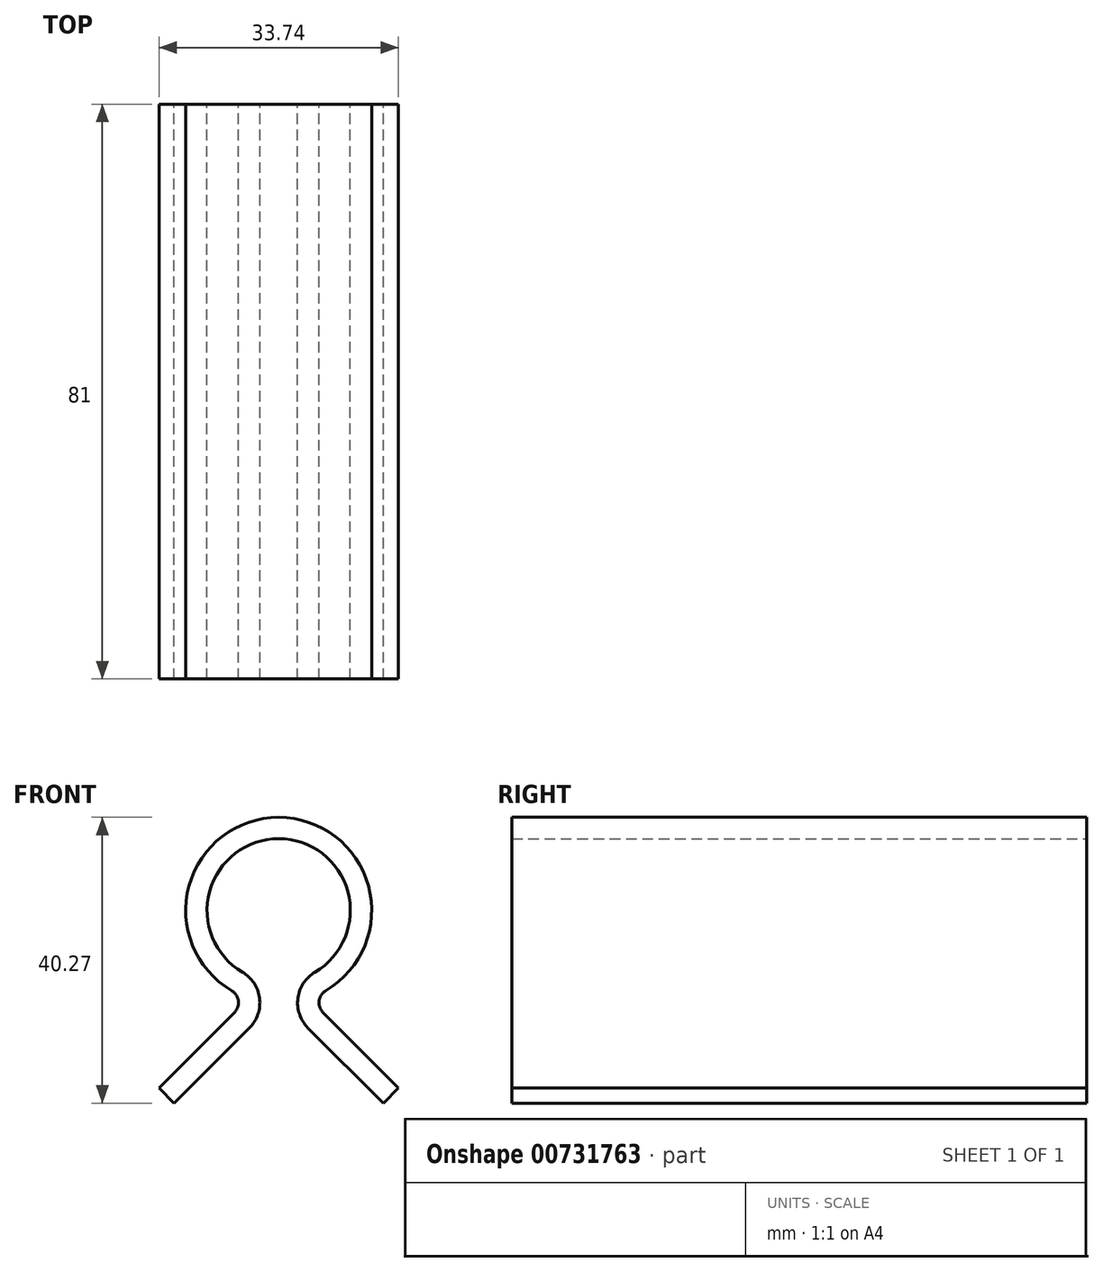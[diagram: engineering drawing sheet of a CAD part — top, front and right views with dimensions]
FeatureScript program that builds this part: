
annotation { "Feature Type Name" : "Feature", "Feature Type Description" : "" }
export const myFeature = defineFeature(function(context is Context, id is Id, definition is map)
    precondition{}
    {
        {
            var Q0;
            Q0=qCreatedBy(makeId("Front.planeOp"),FACE);
            var sketch = newSketch(context, id + "F0", { "sketchPlane" : qUnion([Q0])});
            skArc(sketch, "E0", {"start": v(5.12, -8.7) * mm, "mid": v(9.74, 2.65) * mm, "end": v(0, 10.1) * mm});
            skLineSegment(sketch, "E1", {"start": v(0, 26.72) * mm, "end": v(0, 0) * mm, "construction": true});
            skLineSegment(sketch, "E2", {"start": v(4.12, -16.55) * mm, "end": v(14.74, -27.16) * mm});
            skLineSegment(sketch, "E3", {"start": v(0, 0) * mm, "end": v(0, -27.72) * mm, "construction": true});
            skPoint(sketch, "E4.visualSharp", {"position": v(-2.7, -9.74) * mm});
            skArc(sketch, "E4.filletArc", {"start": v(5.12, -8.7) * mm, "mid": v(2.7, -12.38) * mm, "end": v(4.12, -16.55) * mm});
            skArc(sketch, "E5.0", {"start": v(6.66, -11.3) * mm, "mid": v(12.65, 3.45) * mm, "end": v(0, 13.1) * mm});
            skLineSegment(sketch, "E5.1", {"start": v(6.26, -14.43) * mm, "end": v(16.87, -25.04) * mm});
            skLineSegment(sketch, "E6", {"start": v(14.74, -27.16) * mm, "end": v(16.87, -25.04) * mm});
            skPoint(sketch, "E7.visualSharp", {"position": v(4.24, -12.4) * mm});
            skArc(sketch, "E7.filletArc", {"start": v(6.66, -11.3) * mm, "mid": v(5.7, -12.76) * mm, "end": v(6.26, -14.43) * mm});
            skArc(sketch, "E8.MirrorCS", {"start": v(-5.12, -8.7) * mm, "mid": v(-9.74, 2.65) * mm, "end": v(0, 10.1) * mm});
            skArc(sketch, "E9.MirrorCS", {"start": v(-6.66, -11.3) * mm, "mid": v(-12.65, 3.45) * mm, "end": v(0, 13.1) * mm});
            skLineSegment(sketch, "E10.MirrorCS", {"start": v(-6.26, -14.43) * mm, "end": v(-16.87, -25.04) * mm});
            skLineSegment(sketch, "E11.MirrorCS", {"start": v(-4.12, -16.55) * mm, "end": v(-14.74, -27.16) * mm});
            skLineSegment(sketch, "E12.MirrorCS", {"start": v(-14.74, -27.16) * mm, "end": v(-16.87, -25.04) * mm});
            skArc(sketch, "E13.MirrorCS", {"start": v(-5.12, -8.7) * mm, "mid": v(-2.7, -12.38) * mm, "end": v(-4.12, -16.55) * mm});
            skArc(sketch, "E14.MirrorCS", {"start": v(-6.66, -11.3) * mm, "mid": v(-5.7, -12.76) * mm, "end": v(-6.26, -14.43) * mm});
            skLineSegment(sketch, "E15", {"start": v(0, 0) * mm, "end": v(5.12, -8.7) * mm, "construction": true});
            skSolve(sketch);
        }
        {
            var Q0;
            Q0=makeQuery(id+"F0.imprint","IMPRINT",FACE,{"disambiguationData":[TD([[makeQuery(id+"F0.imprint","IMPRINT",EDGE,{"derivedFrom":sQuery(id+"F0.wireOp",EDGE,"E0")}),-1.0]])]});
            extrude(context, id + "F1", {"entities" : qUnion([Q0]), "depth" : 81 * mm, "offsetDistance" : 25 * mm});
        }
    });
